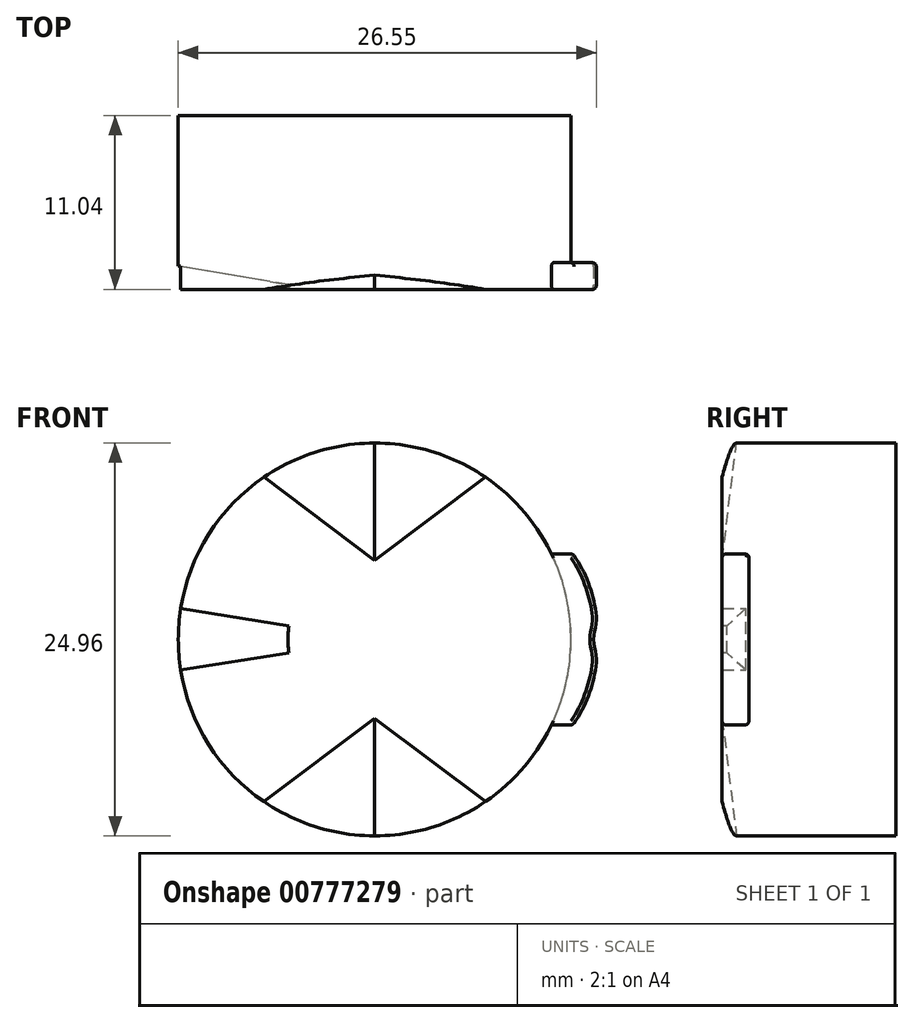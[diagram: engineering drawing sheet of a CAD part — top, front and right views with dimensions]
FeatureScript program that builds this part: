
annotation { "Feature Type Name" : "Feature", "Feature Type Description" : "" }
export const myFeature = defineFeature(function(context is Context, id is Id, definition is map)
    precondition{}
    {
        {
            var Q0;
            Q0=qCreatedBy(makeId("Front.planeOp"),FACE);
            var sketch = newSketch(context, id + "F0", { "sketchPlane" : qUnion([Q0])});
            skCircle(sketch, "E0", {"center": v(0, 0) * mm, "radius": 12.47 * mm});
            skSolve(sketch);
        }
        {
            var Q0;
            Q0=makeQuery(id+"F0.imprint","IMPRINT",FACE,{"disambiguationData":[TD([[makeQuery(id+"F0.imprint","IMPRINT",EDGE,{"derivedFrom":sQuery(id+"F0.wireOp",EDGE,"E0")}),1.0]])]});
            extrude(context, id + "F1", {"entities" : qUnion([Q0]), "depth" : 3.04 * mm, "offsetDistance" : 25 * mm});
        }
        {
            var Q0;
            Q0=makeQuery(id+"F1.opExtrude","CAP_FACE",FACE,{"disambiguationData":[OSD([sQuery(id+"F0.wireOp",EDGE,"E0")])],"isStart":false});
            var sketch = newSketch(context, id + "F2", { "sketchPlane" : qUnion([Q0])});
            skLineSegment(sketch, "E1", {"start": v(0, 0) * mm, "end": v(-7.03, 10.3) * mm, "construction": true});
            skLineSegment(sketch, "E2", {"start": v(0, 0) * mm, "end": v(0, 12.47) * mm, "construction": true});
            skLineSegment(sketch, "E3.MirrorCS", {"start": v(0, 0) * mm, "end": v(7.03, 10.3) * mm, "construction": true});
            skLineSegment(sketch, "E4", {"start": v(0, 0) * mm, "end": v(12.47, 0) * mm, "construction": true});
            skLineSegment(sketch, "E5.MirrorCS", {"start": v(0, 0) * mm, "end": v(7.03, -10.3) * mm, "construction": true});
            skLineSegment(sketch, "E6.MirrorCS", {"start": v(0, 0) * mm, "end": v(-7.03, -10.3) * mm, "construction": true});
            skLineSegment(sketch, "E7", {"start": v(11.42, -5.02) * mm, "end": v(-11.42, -5.02) * mm, "construction": true});
            skLineSegment(sketch, "E8", {"start": v(0, -5.02) * mm, "end": v(0, -12.47) * mm, "construction": true});
            skLineSegment(sketch, "E9", {"start": v(-7.03, -10.3) * mm, "end": v(0, -5.02) * mm});
            skLineSegment(sketch, "E10", {"start": v(7.03, -10.3) * mm, "end": v(0, -5.02) * mm, "construction": true});
            skLineSegment(sketch, "E11.MirrorCS", {"start": v(7.03, 10.3) * mm, "end": v(0, 5.02) * mm, "construction": true});
            skLineSegment(sketch, "E12.MirrorCS", {"start": v(-7.03, 10.3) * mm, "end": v(0, 5.02) * mm, "construction": true});
            skLineSegment(sketch, "E13", {"start": v(0, -5.02) * mm, "end": v(0, -12.47) * mm});
            skArc(sketch, "E14", {"start": v(0, -12.47) * mm, "mid": v(-3.68, -11.92) * mm, "end": v(-7.03, -10.3) * mm});
            skSolve(sketch);
        }
        {
            var Q0;
            Q0=qCreatedBy(makeId("Right.planeOp"),FACE);
            var sketch = newSketch(context, id + "F3", { "sketchPlane" : qUnion([Q0])});
            skLineSegment(sketch, "E15.0", {"start": v(-3.04, -5.02) * mm, "end": v(-3.04, -12.47) * mm});
            skLineSegment(sketch, "E16", {"start": v(-3.04, -12.47) * mm, "end": v(-2.14, -12.47) * mm});
            skLineSegment(sketch, "E17", {"start": v(-2.14, -12.47) * mm, "end": v(-3.04, -5.02) * mm});
            skLineSegment(sketch, "E18", {"start": v(-3.04, -5.02) * mm, "end": v(-7.03, -5.02) * mm, "construction": true});
            skPoint(sketch, "E19.0", {"position": v(-3.04, 0) * mm});
            skLineSegment(sketch, "E20", {"start": v(-3.04, 0) * mm, "end": v(-13.95, 0) * mm});
            skLineSegment(sketch, "E21.MirrorCS", {"start": v(-3.04, 12.47) * mm, "end": v(-2.14, 12.47) * mm});
            skLineSegment(sketch, "E22.0", {"start": v(-3.04, 0) * mm, "end": v(-3.04, 12.47) * mm});
            skPoint(sketch, "E23.0", {"position": v(-3.04, 7.66) * mm});
            skLineSegment(sketch, "E24.0", {"start": v(-3.04, 10.3) * mm, "end": v(-3.04, 5.02) * mm});
            skLineSegment(sketch, "E25", {"start": v(-3.04, 5.02) * mm, "end": v(-2.14, 12.47) * mm});
            skLineSegment(sketch, "E26", {"start": v(-3.04, 10.3) * mm, "end": v(-2.4, 10.3) * mm});
            skSolve(sketch);
        }
        {
            var Q0;
            Q0=sQuery(id+"F2.wireOp",EDGE,"E7");
            cPoint(context, id + "F4", {"entities" : qUnion([Q0]), "parameter" : 0.5});
        }
        {
            var Q0;
            Q0 = qCreatedBy(id + "F4" ,VERTEX);
            var Q1;
            Q1=sQuery(id+"F2.wireOp",VERTEX,"E6.MirrorCS.end");
            var Q2;
            Q2=sQuery(id+"F3.wireOp",VERTEX,"E16.end");
            cPlane(context, id + "F5", {"entities" : qUnion([Q0, Q1, Q2]), "cplaneType" : CPlaneType.THREE_POINT, "offset" : 25 * mm, "width" : 150 * mm, "height" : 150 * mm});
        }
        {
            var Q0;
            Q0 = qSketchRegion(id + "F2", true);
            var Q1;
            Q1=qCreatedBy(id+"F5.planeOp",FACE);
            extrude(context, id + "F6", {"entities" : qUnion([Q0]), "operationType" : NewBodyOperationType.REMOVE, "endBound" : BoundingType.UP_TO_SURFACE, "oppositeDirection" : true, "depth" : 25 * mm, "endBoundEntityFace" : qUnion([Q1]), "offsetDistance" : 25 * mm});
        }
        {
            var Q0;
            Q0=sQuery(id+"F2.wireOp",VERTEX,"E8.start");
            var Q1;
            Q1=makeQuery(id+"F6.boolean.opBoolean","COPY",VERTEX,{"derivedFrom":makeQuery(id+"F6.opExtrude","CAP_VERTEX",VERTEX,{"disambiguationData":[OSD([sQuery(id+"F0.wireOp",EDGE,"E0"),sQuery(id+"F2.wireOp",EDGE,"E13"),sQuery(id+"F2.wireOp",EDGE,"E14"),dummyQuery(id+"F5.planeOp",FACE)])],"isStart":false})});
            var Q2;
            Q2=sQuery(id+"F2.wireOp",VERTEX,"E5.MirrorCS.end");
            cPlane(context, id + "F7", {"entities" : qUnion([Q0, Q1, Q2]), "cplaneType" : CPlaneType.THREE_POINT, "offset" : 25 * mm, "width" : 150 * mm, "height" : 150 * mm});
        }
        {
            var Q0;
            {var subQ0=sQuery(id+"F2.wireOp",EDGE,"E9");Q0=makeQuery(id+"F2.imprint","IMPRINT",FACE,{"disambiguationData":[TD([[makeQuery(id+"F2.imprint","IMPRINT",EDGE,{"derivedFrom":subQ0}),1.0]])]});}
            var sketch = newSketch(context, id + "F8", { "sketchPlane" : qUnion([Q0])});
            skLineSegment(sketch, "E27.0", {"start": v(7.03, -10.3) * mm, "end": v(0, -5.02) * mm});
            skLineSegment(sketch, "E28.0", {"start": v(0, -5.02) * mm, "end": v(0, -12.47) * mm});
            skArc(sketch, "E29", {"start": v(7.03, -10.3) * mm, "mid": v(3.68, -11.92) * mm, "end": v(0, -12.48) * mm});
            skSolve(sketch);
        }
        {
            var Q0;
            Q0 = qSketchRegion(id + "F8", true);
            var Q1;
            Q1=qCreatedBy(id+"F7.planeOp",FACE);
            extrude(context, id + "F9", {"entities" : qUnion([Q0]), "operationType" : NewBodyOperationType.REMOVE, "endBound" : BoundingType.UP_TO_SURFACE, "oppositeDirection" : true, "depth" : 25 * mm, "endBoundEntityFace" : qUnion([Q1]), "offsetDistance" : 25 * mm});
        }
        {
            var Q0;
            Q0=sQuery(id+"F3.wireOp",VERTEX,"E26.end");
            var Q1;
            Q1=sQuery(id+"F2.wireOp",VERTEX,"E1.end");
            var Q2;
            Q2=sQuery(id+"F2.wireOp",VERTEX,"E3.MirrorCS.end");
            cPlane(context, id + "F10", {"entities" : qUnion([Q0, Q1, Q2]), "cplaneType" : CPlaneType.THREE_POINT, "offset" : 25 * mm, "width" : 150 * mm, "height" : 150 * mm});
        }
        {
            var Q0;
            Q0=qCreatedBy(id+"F10.planeOp",FACE);
            var sketch = newSketch(context, id + "F11", { "sketchPlane" : qUnion([Q0])});
            skPoint(sketch, "E30.0", {"position": v(7.03, 3.04) * mm});
            skPoint(sketch, "E31.0", {"position": v(0, 2.4) * mm});
            skPoint(sketch, "E32.0", {"position": v(-7.03, 3.04) * mm});
            skLineSegment(sketch, "E33", {"start": v(0, 2.4) * mm, "end": v(7.03, 3.04) * mm});
            skLineSegment(sketch, "E34", {"start": v(-7.03, 3.04) * mm, "end": v(0, 2.4) * mm});
            skLineSegment(sketch, "E35", {"start": v(-7.03, 3.04) * mm, "end": v(7.03, 3.04) * mm});
            skSolve(sketch);
        }
        {
            var Q0;
            Q0=qCreatedBy(makeId("Right.planeOp"),FACE);
            var sketch = newSketch(context, id + "F12", { "sketchPlane" : qUnion([Q0])});
            skPoint(sketch, "E36.0", {"position": v(-2.4, 10.3) * mm});
            skPoint(sketch, "E37.0", {"position": v(-3.04, 5.02) * mm});
            skLineSegment(sketch, "E38", {"start": v(-3.04, 5.02) * mm, "end": v(-2.4, 10.3) * mm});
            skPoint(sketch, "E39.0", {"position": v(-2.14, 12.47) * mm});
            skLineSegment(sketch, "E40", {"start": v(-2.4, 10.3) * mm, "end": v(-2.14, 12.47) * mm});
            skSolve(sketch);
        }
        {
            var Q0;
            Q0=sQuery(id+"F12.wireOp",VERTEX,"E39.0");
            var Q1;
            Q1=sQuery(id+"F12.wireOp",VERTEX,"E37.0");
            var Q2;
            Q2=sQuery(id+"F11.wireOp",VERTEX,"E32.0");
            cPlane(context, id + "F13", {"entities" : qUnion([Q0, Q1, Q2]), "cplaneType" : CPlaneType.THREE_POINT, "offset" : 25 * mm, "width" : 150 * mm, "height" : 150 * mm});
        }
        {
            var Q0;
            Q0=sQuery(id+"F12.wireOp",VERTEX,"E39.0");
            var Q1;
            Q1=sQuery(id+"F12.wireOp",VERTEX,"E37.0");
            var Q2;
            Q2=sQuery(id+"F11.wireOp",VERTEX,"E30.0");
            cPlane(context, id + "F14", {"entities" : qUnion([Q0, Q1, Q2]), "cplaneType" : CPlaneType.THREE_POINT, "offset" : 25 * mm, "width" : 150 * mm, "height" : 150 * mm});
        }
        {
            var Q0;
            {var subQ0=sQuery(id+"F2.wireOp",EDGE,"E9");Q0=makeQuery(id+"F2.imprint","IMPRINT",FACE,{"disambiguationData":[TD([[makeQuery(id+"F2.imprint","IMPRINT",EDGE,{"derivedFrom":subQ0}),1.0]])]});}
            var sketch = newSketch(context, id + "F15", { "sketchPlane" : qUnion([Q0])});
            skLineSegment(sketch, "E41.0", {"start": v(7.03, 10.3) * mm, "end": v(0, 5.02) * mm});
            skPoint(sketch, "E42.0", {"position": v(0, 12.47) * mm});
            skLineSegment(sketch, "E43", {"start": v(0, 5.02) * mm, "end": v(0, 12.47) * mm});
            skArc(sketch, "E44", {"start": v(7.03, 10.3) * mm, "mid": v(3.68, 11.92) * mm, "end": v(0, 12.48) * mm});
            skSolve(sketch);
        }
        {
            var Q0;
            Q0 = qSketchRegion(id + "F15", true);
            var Q1;
            Q1=qCreatedBy(id+"F14.planeOp",FACE);
            extrude(context, id + "F16", {"entities" : qUnion([Q0]), "operationType" : NewBodyOperationType.REMOVE, "endBound" : BoundingType.UP_TO_SURFACE, "oppositeDirection" : true, "depth" : 25 * mm, "endBoundEntityFace" : qUnion([Q1]), "offsetDistance" : 25 * mm});
        }
        {
            var Q0;
            {var subQ0=sQuery(id+"F2.wireOp",EDGE,"E9");Q0=makeQuery(id+"F2.imprint","IMPRINT",FACE,{"disambiguationData":[TD([[makeQuery(id+"F2.imprint","IMPRINT",EDGE,{"derivedFrom":subQ0}),1.0]])]});}
            var sketch = newSketch(context, id + "F17", { "sketchPlane" : qUnion([Q0])});
            skLineSegment(sketch, "E45.0", {"start": v(-7.03, 10.3) * mm, "end": v(0, 5.02) * mm});
            skPoint(sketch, "E46.0", {"position": v(0, 12.47) * mm});
            skLineSegment(sketch, "E47", {"start": v(0, 5.02) * mm, "end": v(0, 12.47) * mm});
            skArc(sketch, "E48", {"start": v(0, 12.47) * mm, "mid": v(-3.68, 11.92) * mm, "end": v(-7.03, 10.3) * mm});
            skSolve(sketch);
        }
        {
            var Q0;
            Q0 = qSketchRegion(id + "F17", true);
            var Q1;
            Q1=qCreatedBy(id+"F13.planeOp",FACE);
            extrude(context, id + "F18", {"entities" : qUnion([Q0]), "operationType" : NewBodyOperationType.REMOVE, "endBound" : BoundingType.UP_TO_SURFACE, "oppositeDirection" : true, "depth" : 25 * mm, "endBoundEntityFace" : qUnion([Q1]), "offsetDistance" : 25 * mm});
        }
        {
            var Q0;
            Q0=makeQuery(id+"F1.opExtrude","CAP_FACE",FACE,{"disambiguationData":[OSD([sQuery(id+"F0.wireOp",EDGE,"E0")])],"isStart":false});
            var sketch = newSketch(context, id + "F19", { "sketchPlane" : qUnion([Q0])});
            skLineSegment(sketch, "E49", {"start": v(0, 0) * mm, "end": v(33.2, 0) * mm, "construction": true});
            skLineSegment(sketch, "E50", {"start": v(17.66, 5.43) * mm, "end": v(11.23, 5.43) * mm, "construction": true});
            skLineSegment(sketch, "E51", {"start": v(11.23, 5.43) * mm, "end": v(12.58, 5.43) * mm});
            skFitSpline(sketch, "E52", {"points": [v(12.58, 5.43) * mm, v(14.07, 1.3) * mm, v(13.9, 0) * mm], "startDerivative": vector(4.4, -5.8) * mm, "endDerivative": vector(0, -4.14) * mm});
            skFitSpline(sketch, "E53.MirrorCS", {"points": [v(12.58, -5.43) * mm, v(14.07, -1.3) * mm, v(13.9, 0) * mm], "startDerivative": vector(4.4, 5.8) * mm, "endDerivative": vector(0, 4.14) * mm});
            skLineSegment(sketch, "E54.MirrorCS", {"start": v(17.66, -5.43) * mm, "end": v(11.23, -5.43) * mm, "construction": true});
            skLineSegment(sketch, "E55", {"start": v(12.58, -5.43) * mm, "end": v(11.23, -5.43) * mm});
            skArc(sketch, "E56", {"start": v(11.23, 5.43) * mm, "mid": v(12.47, 0) * mm, "end": v(11.23, -5.43) * mm});
            skSolve(sketch);
        }
        {
            var Q0;
            Q0=makeQuery(id+"F19.imprint","IMPRINT",FACE,{"disambiguationData":[TD([[makeQuery(id+"F19.imprint","IMPRINT",EDGE,{"derivedFrom":sQuery(id+"F19.wireOp",EDGE,"E51")}),-1.0]])]});
            extrude(context, id + "F20", {"entities" : qUnion([Q0]), "operationType" : NewBodyOperationType.ADD, "oppositeDirection" : true, "depth" : 1.7 * mm, "offsetDistance" : 25 * mm});
        }
        {
            var Q0;
            {var subQ0=sQuery(id+"F19.wireOp",EDGE,"E56");var subQ1=sQuery(id+"F19.wireOp",EDGE,"E55");var subQ2=sQuery(id+"F19.wireOp",EDGE,"E53.MirrorCS");var subQ3=sQuery(id+"F19.wireOp",EDGE,"E52");var subQ4=sQuery(id+"F19.wireOp",EDGE,"E51");Q0=makeQuery(id+"FGMiUAum6pMF5fA_1.1.F20.boolean.opBoolean","MERGE",FACE,{"derivedFrom":[makeQuery(id+"F20.boolean.opBoolean","MERGE",FACE,{"derivedFrom":[makeQuery(id+"F1.opExtrude","CAP_FACE",FACE,{"disambiguationData":[OSD([sQuery(id+"F0.wireOp",EDGE,"E0")])],"isStart":false}),makeQuery(id+"F20.opExtrude","CAP_FACE",FACE,{"disambiguationData":[OSD([subQ4,subQ3,subQ2,subQ1,subQ0])],"isStart":true})]}),makeQuery(id+"FGMiUAum6pMF5fA_1.1.F20.opExtrude","CAP_FACE",FACE,{"disambiguationData":[OSD([subQ4,subQ3,subQ2,subQ1,subQ0])],"isStart":true})]});}
            var sketch = newSketch(context, id + "F21", { "sketchPlane" : qUnion([Q0])});
            skCircle(sketch, "E57", {"center": v(0, 0) * mm, "radius": 12.47 * mm, "construction": true});
            skLineSegment(sketch, "E58", {"start": v(12.47, 0) * mm, "end": v(-12.47, 0) * mm, "construction": true});
            skLineSegment(sketch, "E59", {"start": v(12.31, 0) * mm, "end": v(12.31, 2) * mm, "construction": true});
            skLineSegment(sketch, "E60", {"start": v(5.51, 0) * mm, "end": v(5.51, 0.7) * mm, "construction": true});
            skLineSegment(sketch, "E61", {"start": v(5.51, 0) * mm, "end": v(5.51, 0.7) * mm});
            skLineSegment(sketch, "E62", {"start": v(12.31, 2) * mm, "end": v(5.51, 0.7) * mm});
            skLineSegment(sketch, "E63.MirrorCS", {"start": v(12.31, -2) * mm, "end": v(5.51, -0.7) * mm});
            skLineSegment(sketch, "E64.MirrorCS", {"start": v(5.51, 0) * mm, "end": v(5.51, -0.7) * mm, "construction": true});
            skArc(sketch, "E65", {"start": v(12.31, 2) * mm, "mid": v(12.47, 0) * mm, "end": v(12.31, -2) * mm});
            skLineSegment(sketch, "E66", {"start": v(0, 0) * mm, "end": v(0, 4.2) * mm, "construction": true});
            skLineSegment(sketch, "E67.MirrorCS", {"start": v(-12.31, 2) * mm, "end": v(-5.51, 0.7) * mm});
            skLineSegment(sketch, "E68.MirrorCS", {"start": v(-5.51, 0) * mm, "end": v(-5.51, 0.7) * mm, "construction": true});
            skLineSegment(sketch, "E69.MirrorCS", {"start": v(-5.51, 0) * mm, "end": v(-5.51, -0.7) * mm, "construction": true});
            skLineSegment(sketch, "E70.MirrorCS", {"start": v(-12.31, -2) * mm, "end": v(-5.51, -0.7) * mm});
            skArc(sketch, "E71.MirrorCS", {"start": v(-12.31, 2) * mm, "mid": v(-12.47, 0) * mm, "end": v(-12.31, -2) * mm});
            skSolve(sketch);
        }
        {
            var Q0;
            Q0=qCreatedBy(makeId("Top.planeOp"),FACE);
            var sketch = newSketch(context, id + "F22", { "sketchPlane" : qUnion([Q0])});
            skPoint(sketch, "E72.0", {"position": v(5.51, -3.04) * mm});
            skPoint(sketch, "E73.0", {"position": v(12.47, -3.04) * mm});
            skPoint(sketch, "E74.0", {"position": v(-5.51, -3.04) * mm});
            skPoint(sketch, "E75.0", {"position": v(-12.47, -3.04) * mm});
            skPoint(sketch, "E76.0", {"position": v(0, -3.04) * mm});
            skLineSegment(sketch, "E77", {"start": v(0, -3.04) * mm, "end": v(0, -11.42) * mm, "construction": true});
            skLineSegment(sketch, "E78", {"start": v(-12.47, -3.04) * mm, "end": v(-12.47, -1.54) * mm});
            skLineSegment(sketch, "E79", {"start": v(-12.47, -1.54) * mm, "end": v(-5.51, -2.74) * mm});
            skLineSegment(sketch, "E80", {"start": v(-5.51, -2.74) * mm, "end": v(-5.51, -3.04) * mm});
            skLineSegment(sketch, "E81", {"start": v(-12.47, -3.04) * mm, "end": v(-5.51, -3.04) * mm});
            skSolve(sketch);
        }
        {
            var Q0;
            Q0 = qSketchRegion(id + "F22", true);
            var Q1;
            Q1=sQuery(id+"F22.wireOp",EDGE,"E77");
            revolve(context, id + "F23", {"operationType" : NewBodyOperationType.REMOVE, "surfaceOperationType" : NewSurfaceOperationType.NEW, "entities" : qUnion([Q0]), "axis" : qUnion([Q1]), "revolveType" : RevolveType.SYMMETRIC, "angle" : 18 * degree});
        }
        {
            var Q0;
            Q0=makeQuery(id+"F6.boolean.opBoolean","COPY",EDGE,{"derivedFrom":makeQuery(id+"F6.opExtrude","TWEAK_EDGE",EDGE,{"derivedFrom":[makeQuery(id+"F2.imprint","IMPRINT",EDGE,{"derivedFrom":sQuery(id+"F2.wireOp",EDGE,"E14")}),dummyQuery(id+"F5.planeOp",FACE)]})});
            var Q1;
            {var subQ5=sQuery(id+"F0.wireOp",EDGE,"E0");var subQ7=makeQuery(id+"F6.boolean.opBoolean","COPY",FACE,{"derivedFrom":makeQuery(id+"F6.opExtrude","CAP_FACE",FACE,{"disambiguationData":[OSD([dummyQuery(id+"F5.planeOp",FACE)])],"isStart":false})});Q1=makeQuery(id+"FGMiUAum6pMF5fA_1.1.F20.boolean.opBoolean","SPLIT",EDGE,{"disambiguationData":[TD([subQ7])],"derivedFrom":makeQuery(id+"F16.boolean.opBoolean","SPLIT",EDGE,{"disambiguationData":[TD([subQ7])],"derivedFrom":makeQuery(id+"F1.opExtrude","CAP_EDGE",EDGE,{"disambiguationData":[OSD([subQ5])],"isStart":false})})});}
            var Q2;
            Q2=makeQuery(id+"FGMiUAum6pMF5fA_1.1.F20.opExtrude","CAP_EDGE",EDGE,{"disambiguationData":[OSD([sQuery(id+"F19.wireOp",EDGE,"E55")])],"isStart":true});
            var Q3;
            Q3=makeQuery(id+"FGMiUAum6pMF5fA_1.1.F20.opExtrude","CAP_EDGE",EDGE,{"disambiguationData":[OSD([sQuery(id+"F19.wireOp",EDGE,"E53.MirrorCS")])],"isStart":true});
            var Q4;
            Q4=makeQuery(id+"FGMiUAum6pMF5fA_1.1.F20.opExtrude","CAP_EDGE",EDGE,{"disambiguationData":[OSD([sQuery(id+"F19.wireOp",EDGE,"E51")])],"isStart":true});
            var Q5;
            {var subQ5=sQuery(id+"F0.wireOp",EDGE,"E0");Q5=makeQuery(id+"FGMiUAum6pMF5fA_1.1.F20.boolean.opBoolean","SPLIT",EDGE,{"disambiguationData":[TD([makeQuery(id+"F18.boolean.opBoolean","COPY",FACE,{"derivedFrom":makeQuery(id+"F18.opExtrude","CAP_FACE",FACE,{"disambiguationData":[OSD([dummyQuery(id+"F13.planeOp",FACE)])],"isStart":false})})])],"derivedFrom":makeQuery(id+"F16.boolean.opBoolean","SPLIT",EDGE,{"disambiguationData":[TD([makeQuery(id+"F6.boolean.opBoolean","COPY",FACE,{"derivedFrom":makeQuery(id+"F6.opExtrude","CAP_FACE",FACE,{"disambiguationData":[OSD([dummyQuery(id+"F5.planeOp",FACE)])],"isStart":false})})])],"derivedFrom":makeQuery(id+"F1.opExtrude","CAP_EDGE",EDGE,{"disambiguationData":[OSD([subQ5])],"isStart":false})})});}
            var Q6;
            Q6=makeQuery(id+"F18.boolean.opBoolean","COPY",EDGE,{"derivedFrom":makeQuery(id+"F18.opExtrude","TWEAK_EDGE",EDGE,{"derivedFrom":[dummyQuery(id+"F13.planeOp",FACE),makeQuery(id+"F17.imprint","IMPRINT",EDGE,{"derivedFrom":sQuery(id+"F17.wireOp",EDGE,"E48")})]})});
            var Q7;
            Q7=makeQuery(id+"F16.boolean.opBoolean","COPY",EDGE,{"derivedFrom":makeQuery(id+"F16.opExtrude","TWEAK_EDGE",EDGE,{"derivedFrom":[dummyQuery(id+"F14.planeOp",FACE),makeQuery(id+"F15.imprint","IMPRINT",EDGE,{"derivedFrom":sQuery(id+"F15.wireOp",EDGE,"E44")})]})});
            var Q8;
            {var subQ0=makeQuery(id+"F16.opExtrude","CAP_FACE",FACE,{"disambiguationData":[OSD([dummyQuery(id+"F14.planeOp",FACE)])],"isStart":false});var subQ2=sQuery(id+"F0.wireOp",EDGE,"E0");Q8=makeQuery(id+"F20.boolean.opBoolean","SPLIT",EDGE,{"disambiguationData":[TD([makeQuery(id+"F16.boolean.opBoolean","COPY",FACE,{"derivedFrom":subQ0})])],"derivedFrom":makeQuery(id+"F16.boolean.opBoolean","SPLIT",EDGE,{"disambiguationData":[TD([makeQuery(id+"F9.boolean.opBoolean","COPY",FACE,{"derivedFrom":makeQuery(id+"F9.opExtrude","CAP_FACE",FACE,{"disambiguationData":[OSD([dummyQuery(id+"F7.planeOp",FACE)])],"isStart":false})})])],"derivedFrom":makeQuery(id+"F1.opExtrude","CAP_EDGE",EDGE,{"disambiguationData":[OSD([subQ2])],"isStart":false})})});}
            var Q9;
            Q9=makeQuery(id+"F20.opExtrude","CAP_EDGE",EDGE,{"disambiguationData":[OSD([sQuery(id+"F19.wireOp",EDGE,"E51")])],"isStart":true});
            var Q10;
            Q10=makeQuery(id+"F20.opExtrude","CAP_EDGE",EDGE,{"disambiguationData":[OSD([sQuery(id+"F19.wireOp",EDGE,"E52")])],"isStart":true});
            var Q11;
            Q11=makeQuery(id+"F20.opExtrude","CAP_EDGE",EDGE,{"disambiguationData":[OSD([sQuery(id+"F19.wireOp",EDGE,"E55")])],"isStart":true});
            var Q12;
            {var subQ1=makeQuery(id+"F9.boolean.opBoolean","COPY",FACE,{"derivedFrom":makeQuery(id+"F9.opExtrude","CAP_FACE",FACE,{"disambiguationData":[OSD([dummyQuery(id+"F7.planeOp",FACE)])],"isStart":false})});var subQ2=sQuery(id+"F0.wireOp",EDGE,"E0");Q12=makeQuery(id+"F20.boolean.opBoolean","SPLIT",EDGE,{"disambiguationData":[TD([subQ1])],"derivedFrom":makeQuery(id+"F16.boolean.opBoolean","SPLIT",EDGE,{"disambiguationData":[TD([subQ1])],"derivedFrom":makeQuery(id+"F1.opExtrude","CAP_EDGE",EDGE,{"disambiguationData":[OSD([subQ2])],"isStart":false})})});}
            var Q13;
            Q13=makeQuery(id+"F9.boolean.opBoolean","COPY",EDGE,{"derivedFrom":makeQuery(id+"F9.opExtrude","TWEAK_EDGE",EDGE,{"derivedFrom":[dummyQuery(id+"F7.planeOp",FACE),makeQuery(id+"F8.imprint","IMPRINT",EDGE,{"derivedFrom":sQuery(id+"F8.wireOp",EDGE,"E29")})]})});
            var Q14;
            Q14=makeQuery(id+"FGMiUAum6pMF5fA_1.1.F20.opExtrude","SWEPT_EDGE",EDGE,{"disambiguationData":[OSD([sQuery(id+"F19.wireOp",EDGE,"E53.MirrorCS"),sQuery(id+"F19.wireOp",EDGE,"E55")])]});
            var Q15;
            Q15=makeQuery(id+"FGMiUAum6pMF5fA_1.1.F20.opExtrude","CAP_EDGE",EDGE,{"disambiguationData":[OSD([sQuery(id+"F19.wireOp",EDGE,"E55")])],"isStart":false});
            var Q16;
            Q16=makeQuery(id+"FGMiUAum6pMF5fA_1.1.F20.opExtrude","CAP_EDGE",EDGE,{"disambiguationData":[OSD([sQuery(id+"F19.wireOp",EDGE,"E53.MirrorCS")])],"isStart":false});
            var Q17;
            Q17=makeQuery(id+"FGMiUAum6pMF5fA_1.1.F20.opExtrude","SWEPT_EDGE",EDGE,{"disambiguationData":[OSD([sQuery(id+"F19.wireOp",EDGE,"E51"),sQuery(id+"F19.wireOp",EDGE,"E52")])]});
            var Q18;
            Q18=makeQuery(id+"FGMiUAum6pMF5fA_1.1.F20.opExtrude","CAP_EDGE",EDGE,{"disambiguationData":[OSD([sQuery(id+"F19.wireOp",EDGE,"E51")])],"isStart":false});
            var Q19;
            Q19=makeQuery(id+"F20.opExtrude","SWEPT_EDGE",EDGE,{"disambiguationData":[OSD([sQuery(id+"F19.wireOp",EDGE,"E51"),sQuery(id+"F19.wireOp",EDGE,"E52")])]});
            var Q20;
            Q20=makeQuery(id+"F20.opExtrude","CAP_EDGE",EDGE,{"disambiguationData":[OSD([sQuery(id+"F19.wireOp",EDGE,"E51")])],"isStart":false});
            var Q21;
            Q21=makeQuery(id+"F20.opExtrude","CAP_EDGE",EDGE,{"disambiguationData":[OSD([sQuery(id+"F19.wireOp",EDGE,"E52")])],"isStart":false});
            var Q22;
            Q22=makeQuery(id+"F20.opExtrude","CAP_EDGE",EDGE,{"disambiguationData":[OSD([sQuery(id+"F19.wireOp",EDGE,"E55")])],"isStart":false});
            var Q23;
            Q23=makeQuery(id+"F20.opExtrude","SWEPT_EDGE",EDGE,{"disambiguationData":[OSD([sQuery(id+"F19.wireOp",EDGE,"E53.MirrorCS"),sQuery(id+"F19.wireOp",EDGE,"E55")])]});
            fillet(context, id + "F24", {"entities" : qUnion([Q0, Q1, Q2, Q3, Q4, Q5, Q6, Q7, Q8, Q9, Q10, Q11, Q12, Q13, Q14, Q15, Q16, Q17, Q18, Q19, Q20, Q21, Q22, Q23]), "radius" : .25 * mm, "tangentPropagation" : true, "allowEdgeOverflow" : false});
        }
        {
            var Q0;
            Q0=makeQuery(id+"F1.opExtrude","CAP_FACE",FACE,{"disambiguationData":[OSD([sQuery(id+"F0.wireOp",EDGE,"E0")])],"isStart":true});
            var sketch = newSketch(context, id + "F25", { "sketchPlane" : qUnion([Q0])});
            skCircle(sketch, "E82.0", {"center": v(0, 0) * mm, "radius": 12.47 * mm});
            skSolve(sketch);
        }
        {
            var Q0;
            Q0=makeQuery(id+"F25.imprint","IMPRINT",FACE,{"disambiguationData":[TD([[makeQuery(id+"F25.imprint","IMPRINT",EDGE,{"derivedFrom":sQuery(id+"F25.wireOp",EDGE,"E82.0")}),-1.0]])]});
            extrude(context, id + "F26", {"entities" : qUnion([Q0]), "operationType" : NewBodyOperationType.ADD, "depth" : 8 * mm, "offsetDistance" : 25 * mm});
        }
    });
